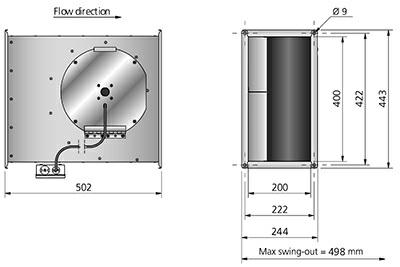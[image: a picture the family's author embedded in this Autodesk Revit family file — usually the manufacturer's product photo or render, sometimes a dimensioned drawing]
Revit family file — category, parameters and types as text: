
# Revit family: RKB 400x200 A1 AC_7470005
name_source: partatom
category: Mechanical Equipment
revit_build: Autodesk Revit MEP 2014 (Build: 20130308_1515(x64)
units: mm (PartAtom-declared; Revit-internal decimal feet)

## types (3) — shared parameters
Connector Height = 200 mm  [stored 0.656168 ft]
Connector Width = 400 mm  [stored 1.31234 ft]
Current = 1 A
Depth = 443 mm  [stored 1.45341 ft]
Description = UNINSULATED DUCT FANS WITH RECTANGULAR CONNECTIONS
Frequency = 50 Hz
Height = 243 mm  [stored 0.797244 ft]
Main Material = Steel, Galvanized
Phase = 1
Voltage = 230 V
Voltage range = 220-240 V
Width = 502 mm  [stored 1.64698 ft]
Wiring diagram = 4040001

## per-type parameters (varying)
| type | Capacitor | Max. temperature of transported air | Max. temperature of transported air when speed controlled | Power | Sound pressure level at 3 m | Speed | Weight |
| RKB 400X200 A1 AC | 3 μF | 70 °C | 70 °C | 115 W | 53 dB(A) | 2530 rpm | 9.80 kg |
| RBK 400X200 B1 ErP AC | 5 μF | 70 °C | 70 °C | 169 W | 58 dB(A) | 2690 rpm | 10.50 kg |
| RBK 400X200 E1 ErP AC | 6 μF | 60 °C | 60 °C | 229 W | 59 dB(A) | 2760 rpm | 11.10 kg |

note: [stored X ft] marks values corroborated as IEEE doubles in the binary element streams (Revit-internal decimal feet)

## geometry (parser evidence)
native form markers: Sweep x4
no freeform markers — native parametric forms only
